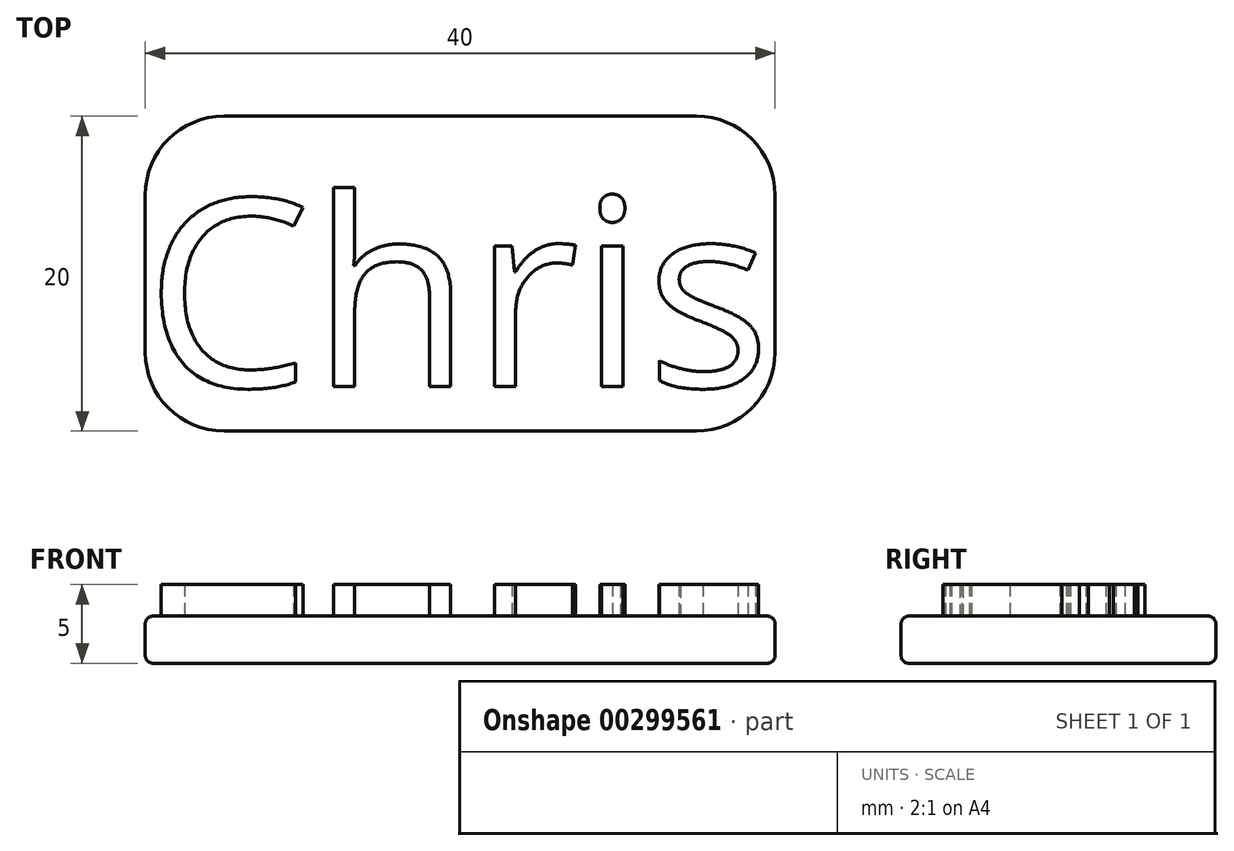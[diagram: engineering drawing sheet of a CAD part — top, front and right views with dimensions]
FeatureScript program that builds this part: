
annotation { "Feature Type Name" : "Feature", "Feature Type Description" : "" }
export const myFeature = defineFeature(function(context is Context, id is Id, definition is map)
    precondition{}
    {
        {
            var Q0;
            Q0=qCreatedBy(makeId("Top.planeOp"),FACE);
            var sketch = newSketch(context, id + "F0", { "sketchPlane" : qUnion([Q0])});
            skLineSegment(sketch, "E0.bottom", {"start": v(-17.7, 17.18) * mm, "end": v(22.3, 17.18) * mm});
            skLineSegment(sketch, "E0.top", {"start": v(-17.7, -2.82) * mm, "end": v(22.3, -2.82) * mm});
            skLineSegment(sketch, "E0.left", {"start": v(-17.7, 17.18) * mm, "end": v(-17.7, -2.82) * mm});
            skLineSegment(sketch, "E0.right", {"start": v(22.3, 17.18) * mm, "end": v(22.3, -2.82) * mm});
            skSolve(sketch);
        }
        {
            var Q0;
            Q0=makeQuery(id+"F0.imprint","IMPRINT",FACE,{"disambiguationData":[TD([[makeQuery(id+"F0.imprint","IMPRINT",EDGE,{"derivedFrom":sQuery(id+"F0.wireOp",EDGE,"E0.bottom")}),-1.0]])]});
            extrude(context, id + "F1", {"entities" : qUnion([Q0]), "depth" : 3 * mm});
        }
        {
            var Q0;
            Q0=makeQuery(id+"F1.opExtrude","CAP_FACE",FACE,{"disambiguationData":[OSD([sQuery(id+"F0.wireOp",EDGE,"E0.bottom"),sQuery(id+"F0.wireOp",EDGE,"E0.top"),sQuery(id+"F0.wireOp",EDGE,"E0.left"),sQuery(id+"F0.wireOp",EDGE,"E0.right")])],"isStart":false});
            var sketch = newSketch(context, id + "F2", { "sketchPlane" : qUnion([Q0])});
            skText(sketch, "E1", { "text": "Chris", "fontName": "OpenSans-Regular.ttf"});
            const initialGuessF2  = {"E1": [-0.0177, 0, 1, 0, 0.012]};
            skSetInitialGuess(sketch, initialGuessF2);
            skSolve(sketch);
        }
        {
            var Q0;
            Q0 = qSketchRegion(id + "F2", true);
            extrude(context, id + "F3", {"entities" : qUnion([Q0]), "operationType" : NewBodyOperationType.ADD, "depth" : 2 * mm});
        }
        {
            var Q0;
            Q0=makeQuery(id+"F1.opExtrude","CAP_EDGE",EDGE,{"disambiguationData":[OSD([sQuery(id+"F0.wireOp",EDGE,"E0.left")])],"isStart":false});
            var Q1;
            Q1=makeQuery(id+"F1.opExtrude","CAP_EDGE",EDGE,{"disambiguationData":[OSD([sQuery(id+"F0.wireOp",EDGE,"E0.top")])],"isStart":false});
            var Q2;
            Q2=makeQuery(id+"F1.opExtrude","CAP_EDGE",EDGE,{"disambiguationData":[OSD([sQuery(id+"F0.wireOp",EDGE,"E0.bottom")])],"isStart":false});
            var Q3;
            Q3=makeQuery(id+"F1.opExtrude","CAP_EDGE",EDGE,{"disambiguationData":[OSD([sQuery(id+"F0.wireOp",EDGE,"E0.right")])],"isStart":false});
            var Q4;
            Q4=makeQuery(id+"F1.opExtrude","CAP_EDGE",EDGE,{"disambiguationData":[OSD([sQuery(id+"F0.wireOp",EDGE,"E0.left")])],"isStart":true});
            var Q5;
            Q5=makeQuery(id+"F1.opExtrude","CAP_EDGE",EDGE,{"disambiguationData":[OSD([sQuery(id+"F0.wireOp",EDGE,"E0.top")])],"isStart":true});
            var Q6;
            Q6=makeQuery(id+"F1.opExtrude","CAP_EDGE",EDGE,{"disambiguationData":[OSD([sQuery(id+"F0.wireOp",EDGE,"E0.bottom")])],"isStart":true});
            var Q7;
            Q7=makeQuery(id+"F1.opExtrude","CAP_EDGE",EDGE,{"disambiguationData":[OSD([sQuery(id+"F0.wireOp",EDGE,"E0.right")])],"isStart":true});
            fillet(context, id + "F4", {"entities" : qUnion([Q0, Q1, Q2, Q3, Q4, Q5, Q6, Q7]), "radius" : .5 * mm, "tangentPropagation" : true, "allowEdgeOverflow" : false});
        }
        {
            var Q0;
            Q0=makeQuery(id+"F1.opExtrude","SWEPT_EDGE",EDGE,{"disambiguationData":[OSD([sQuery(id+"F0.wireOp",EDGE,"E0.bottom"),sQuery(id+"F0.wireOp",EDGE,"E0.right")])]});
            var Q1;
            Q1=makeQuery(id+"F1.opExtrude","SWEPT_EDGE",EDGE,{"disambiguationData":[OSD([sQuery(id+"F0.wireOp",EDGE,"E0.top"),sQuery(id+"F0.wireOp",EDGE,"E0.right")])]});
            var Q2;
            Q2=makeQuery(id+"F1.opExtrude","SWEPT_EDGE",EDGE,{"disambiguationData":[OSD([sQuery(id+"F0.wireOp",EDGE,"E0.top"),sQuery(id+"F0.wireOp",EDGE,"E0.left")])]});
            var Q3;
            Q3=makeQuery(id+"F1.opExtrude","SWEPT_EDGE",EDGE,{"disambiguationData":[OSD([sQuery(id+"F0.wireOp",EDGE,"E0.bottom"),sQuery(id+"F0.wireOp",EDGE,"E0.left")])]});
            fillet(context, id + "F5", {"entities" : qUnion([Q0, Q1, Q2, Q3]), "radius" : 5 * mm, "tangentPropagation" : true, "allowEdgeOverflow" : false});
        }
    });
